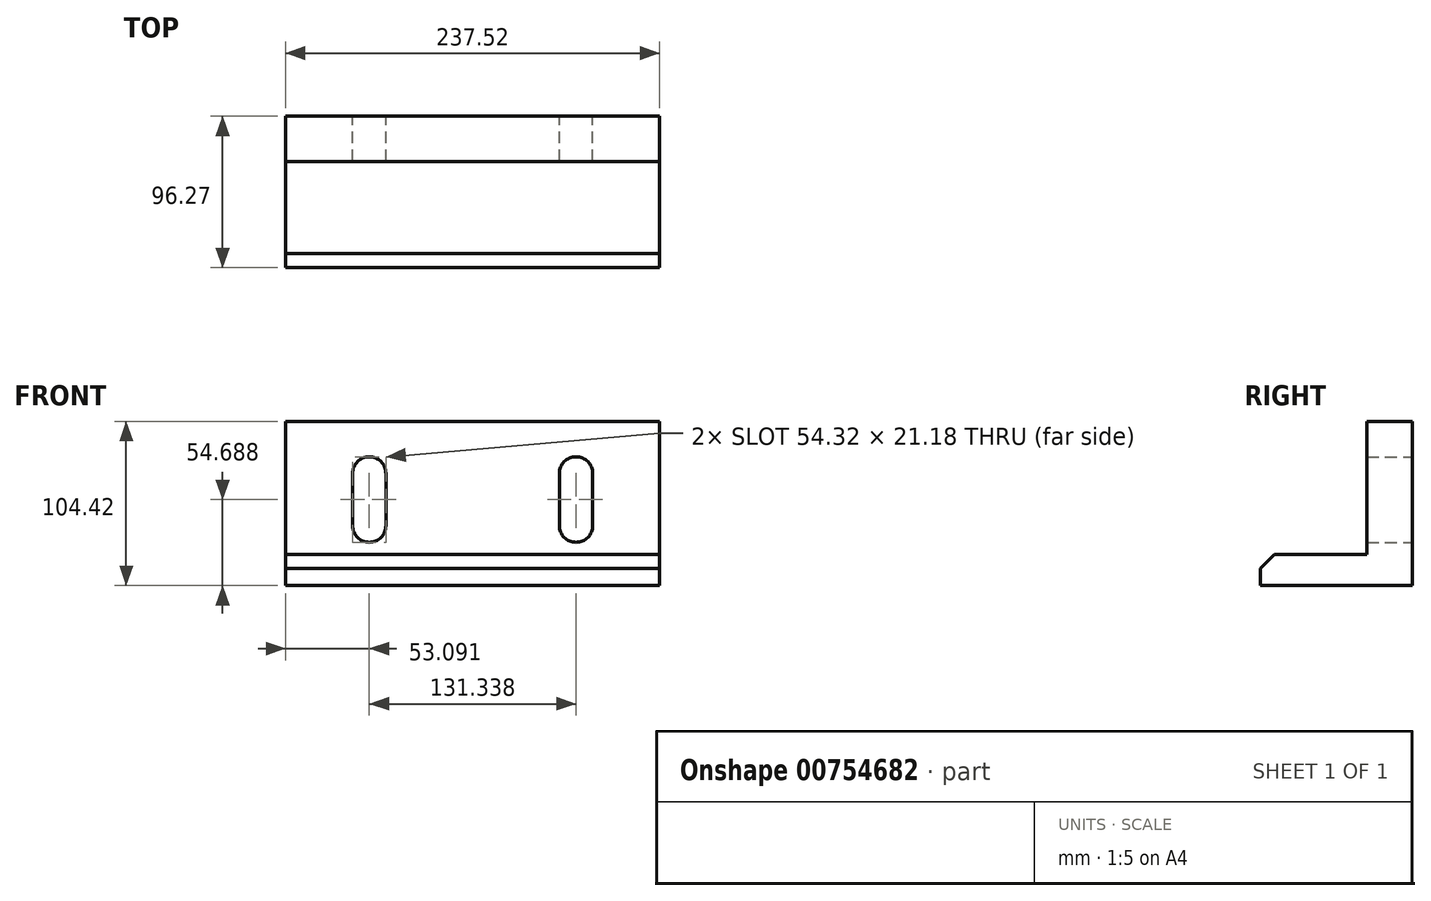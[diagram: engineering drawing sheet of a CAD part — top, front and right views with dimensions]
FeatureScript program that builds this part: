
annotation { "Feature Type Name" : "Feature", "Feature Type Description" : "" }
export const myFeature = defineFeature(function(context is Context, id is Id, definition is map)
    precondition{}
    {
        {
            var Q0;
            Q0=qCreatedBy(makeId("Front.planeOp"),FACE);
            var sketch = newSketch(context, id + "F0", { "sketchPlane" : qUnion([Q0])});
            skLineSegment(sketch, "E0.bottom", {"start": v(-118.76, 0) * mm, "end": v(118.76, 0) * mm});
            skLineSegment(sketch, "E0.top", {"start": v(-118.76, -104.42) * mm, "end": v(118.76, -104.42) * mm});
            skLineSegment(sketch, "E0.left", {"start": v(-118.76, 0) * mm, "end": v(-118.76, -104.42) * mm});
            skLineSegment(sketch, "E0.right", {"start": v(118.76, 0) * mm, "end": v(118.76, -104.42) * mm});
            skLineSegment(sketch, "E1", {"start": v(0, 0) * mm, "end": v(0, -104.42) * mm, "construction": true});
            skArc(sketch, "E2", {"start": v(-55.08, -33.17) * mm, "mid": v(-65.67, -22.57) * mm, "end": v(-76.26, -33.17) * mm});
            skArc(sketch, "E3", {"start": v(-76.26, -66.3) * mm, "mid": v(-65.67, -76.9) * mm, "end": v(-55.08, -66.3) * mm});
            skLineSegment(sketch, "E4", {"start": v(-65.67, -33.17) * mm, "end": v(-65.67, -66.3) * mm, "construction": true});
            skArc(sketch, "E5.MirrorC", {"start": v(-76.26, -33.17) * mm, "mid": v(-65.67, -22.57) * mm, "end": v(-55.08, -33.17) * mm});
            skArc(sketch, "E6.MirrorC", {"start": v(-55.08, -66.3) * mm, "mid": v(-65.67, -76.9) * mm, "end": v(-76.26, -66.3) * mm});
            skLineSegment(sketch, "E7", {"start": v(-76.26, -33.17) * mm, "end": v(-76.26, -66.3) * mm});
            skLineSegment(sketch, "E8.MirrorCS", {"start": v(-55.08, -33.17) * mm, "end": v(-55.08, -66.3) * mm});
            skArc(sketch, "E9.MirrorCS", {"start": v(55.08, -33.17) * mm, "mid": v(65.67, -22.57) * mm, "end": v(76.26, -33.17) * mm});
            skArc(sketch, "E10.MirrorCS", {"start": v(76.26, -66.3) * mm, "mid": v(65.67, -76.9) * mm, "end": v(55.08, -66.3) * mm});
            skLineSegment(sketch, "E11.MirrorCS", {"start": v(76.26, -33.17) * mm, "end": v(76.26, -66.3) * mm});
            skLineSegment(sketch, "E12.MirrorCS", {"start": v(55.08, -33.17) * mm, "end": v(55.08, -66.3) * mm});
            skLineSegment(sketch, "E13.MirrorCS", {"start": v(65.67, -33.17) * mm, "end": v(65.67, -66.3) * mm, "construction": true});
            skArc(sketch, "E14.MirrorCS", {"start": v(76.26, -33.17) * mm, "mid": v(65.67, -22.57) * mm, "end": v(55.08, -33.17) * mm});
            skArc(sketch, "E15.MirrorCS", {"start": v(55.08, -66.3) * mm, "mid": v(65.67, -76.9) * mm, "end": v(76.26, -66.3) * mm});
            skSolve(sketch);
        }
        {
            var Q0;
            Q0 = qSketchRegion(id + "F0", true);
            extrude(context, id + "F1", {"entities" : qUnion([Q0]), "depth" : 28.7 * mm, "offsetDistance" : 25.4 * mm});
        }
        {
            var Q0;
            Q0=makeQuery(id+"F1.opExtrude","CAP_FACE",FACE,{"disambiguationData":[OSD([sQuery(id+"F0.wireOp",EDGE,"E0.bottom"),sQuery(id+"F0.wireOp",EDGE,"E0.top"),sQuery(id+"F0.wireOp",EDGE,"E0.left"),sQuery(id+"F0.wireOp",EDGE,"E0.right"),sQuery(id+"F0.wireOp",EDGE,"E5.MirrorC"),sQuery(id+"F0.wireOp",EDGE,"E6.MirrorC"),sQuery(id+"F0.wireOp",EDGE,"E7"),sQuery(id+"F0.wireOp",EDGE,"E8.MirrorCS"),sQuery(id+"F0.wireOp",EDGE,"E11.MirrorCS"),sQuery(id+"F0.wireOp",EDGE,"E12.MirrorCS"),sQuery(id+"F0.wireOp",EDGE,"E14.MirrorCS"),sQuery(id+"F0.wireOp",EDGE,"E15.MirrorCS")])],"isStart":false});
            var sketch = newSketch(context, id + "F2", { "sketchPlane" : qUnion([Q0])});
            skLineSegment(sketch, "E16.bottom", {"start": v(-118.76, -104.42) * mm, "end": v(118.76, -104.42) * mm});
            skLineSegment(sketch, "E16.top", {"start": v(-118.76, -84.5) * mm, "end": v(118.76, -84.5) * mm});
            skLineSegment(sketch, "E16.left", {"start": v(-118.76, -104.42) * mm, "end": v(-118.76, -84.5) * mm});
            skLineSegment(sketch, "E16.right", {"start": v(118.76, -104.42) * mm, "end": v(118.76, -84.5) * mm});
            skSolve(sketch);
        }
        {
            var Q0;
            Q0 = qSketchRegion(id + "F2", true);
            extrude(context, id + "F3", {"entities" : qUnion([Q0]), "operationType" : NewBodyOperationType.ADD, "depth" : 67.56 * mm, "offsetDistance" : 25.4 * mm});
        }
        {
            var Q0;
            Q0=makeQuery(id+"F3.opExtrude","CAP_EDGE",EDGE,{"disambiguationData":[OSD([sQuery(id+"F2.wireOp",EDGE,"E16.top")])],"isStart":false});
            chamfer(context, id + "F4", {"entities" : qUnion([Q0]), "chamferType" : ChamferType.OFFSET_ANGLE, "width" : 8.9 * mm, "oppositeDirection" : false, "angle" : 45 * degree, "tangentPropagation" : true});
        }
    });
